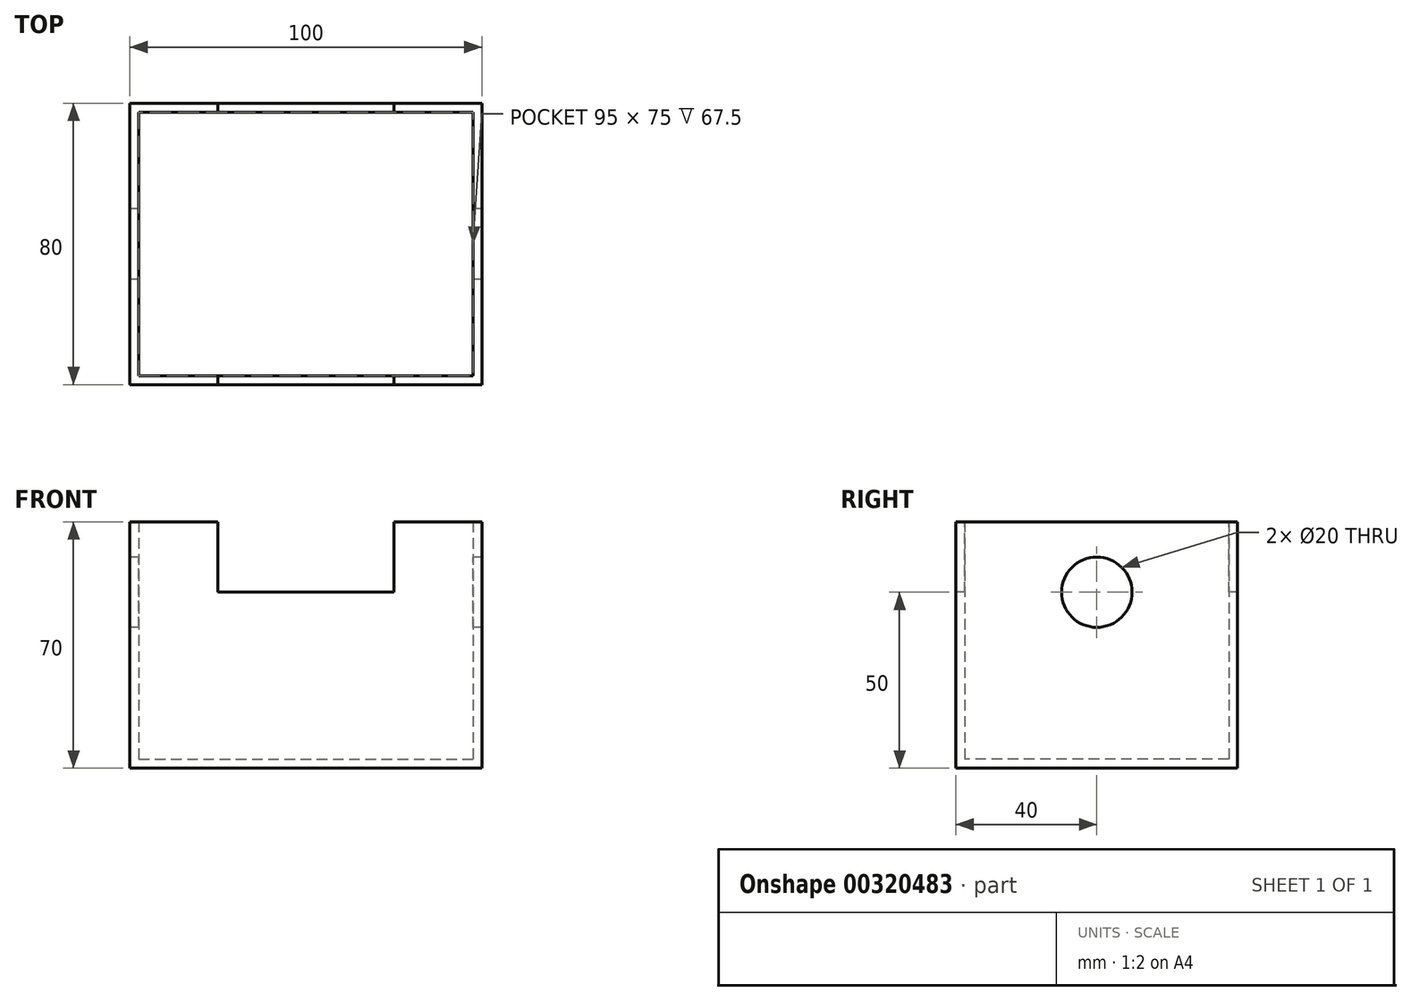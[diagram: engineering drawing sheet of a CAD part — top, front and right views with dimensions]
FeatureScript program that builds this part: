
annotation { "Feature Type Name" : "Feature", "Feature Type Description" : "" }
export const myFeature = defineFeature(function(context is Context, id is Id, definition is map)
    precondition{}
    {
        {
            var Q0;
            Q0=qCreatedBy(makeId("Top.planeOp"),FACE);
            var sketch = newSketch(context, id + "F0", { "sketchPlane" : qUnion([Q0])});
            skLineSegment(sketch, "E0.bottom", {"start": v(-50, 40) * mm, "end": v(50, 40) * mm});
            skLineSegment(sketch, "E0.top", {"start": v(-50, -40) * mm, "end": v(50, -40) * mm});
            skLineSegment(sketch, "E0.left", {"start": v(-50, 40) * mm, "end": v(-50, -40) * mm});
            skLineSegment(sketch, "E0.right", {"start": v(50, 40) * mm, "end": v(50, -40) * mm});
            skSolve(sketch);
        }
        {
            var Q0;
            Q0=makeQuery(id+"F0.imprint","IMPRINT",FACE,{"disambiguationData":[TD([[makeQuery(id+"F0.imprint","IMPRINT",EDGE,{"derivedFrom":sQuery(id+"F0.wireOp",EDGE,"E0.bottom")}),-1.0]])]});
            extrude(context, id + "F1", {"entities" : qUnion([Q0]), "depth" : 70 * mm});
        }
        {
            var Q0;
            Q0=makeQuery(id+"F1.opExtrude","CAP_FACE",FACE,{"disambiguationData":[OSD([sQuery(id+"F0.wireOp",EDGE,"E0.bottom"),sQuery(id+"F0.wireOp",EDGE,"E0.top"),sQuery(id+"F0.wireOp",EDGE,"E0.left"),sQuery(id+"F0.wireOp",EDGE,"E0.right")])],"isStart":false});
            shell(context, id + "F2", {"entities" : qUnion([Q0]), "thickness" : 2.5 * mm});
        }
        {
            var Q0;
            Q0=makeQuery(id+"F1.opExtrude","SWEPT_FACE",FACE,{"disambiguationData":[OSD([sQuery(id+"F0.wireOp",EDGE,"E0.top")])]});
            var sketch = newSketch(context, id + "F3", { "sketchPlane" : qUnion([Q0])});
            skLineSegment(sketch, "E1.bottom", {"start": v(-25, 70) * mm, "end": v(25, 70) * mm});
            skLineSegment(sketch, "E1.top", {"start": v(-25, 50) * mm, "end": v(25, 50) * mm});
            skLineSegment(sketch, "E1.left", {"start": v(-25, 70) * mm, "end": v(-25, 50) * mm});
            skLineSegment(sketch, "E1.right", {"start": v(25, 70) * mm, "end": v(25, 50) * mm});
            skSolve(sketch);
        }
        {
            var Q0;
            Q0=makeQuery(id+"F3.imprint","IMPRINT",FACE,{"disambiguationData":[TD([[makeQuery(id+"F3.imprint","IMPRINT",EDGE,{"derivedFrom":sQuery(id+"F3.wireOp",EDGE,"E1.bottom")}),-1.0]])]});
            extrude(context, id + "F4", {"entities" : qUnion([Q0]), "operationType" : NewBodyOperationType.REMOVE, "endBound" : BoundingType.THROUGH_ALL, "oppositeDirection" : true, "depth" : 25 * mm});
        }
        {
            var Q0;
            Q0=makeQuery(id+"F1.opExtrude","SWEPT_FACE",FACE,{"disambiguationData":[OSD([sQuery(id+"F0.wireOp",EDGE,"E0.left")])]});
            var sketch = newSketch(context, id + "F5", { "sketchPlane" : qUnion([Q0])});
            skCircle(sketch, "E2", {"center": v(0, 50) * mm, "radius": 10 * mm});
            skSolve(sketch);
        }
        {
            var Q0;
            Q0=makeQuery(id+"F5.imprint","IMPRINT",FACE,{"disambiguationData":[TD([[makeQuery(id+"F5.imprint","IMPRINT",EDGE,{"derivedFrom":sQuery(id+"F5.wireOp",EDGE,"E2")}),1.0]])]});
            extrude(context, id + "F6", {"entities" : qUnion([Q0]), "operationType" : NewBodyOperationType.REMOVE, "endBound" : BoundingType.THROUGH_ALL, "oppositeDirection" : true, "depth" : 25 * mm});
        }
    });
